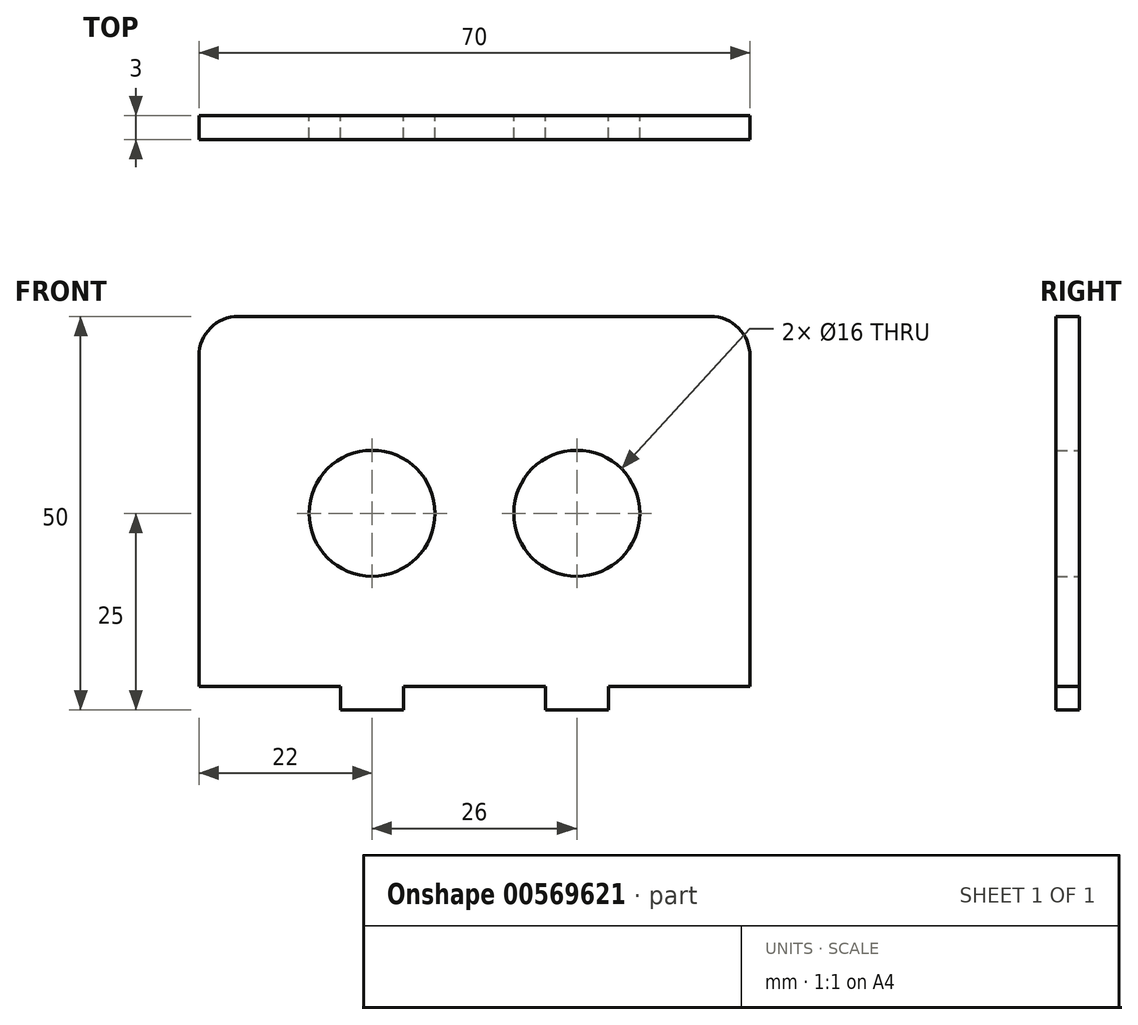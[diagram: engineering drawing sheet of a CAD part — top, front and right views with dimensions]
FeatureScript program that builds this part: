
annotation { "Feature Type Name" : "Feature", "Feature Type Description" : "" }
export const myFeature = defineFeature(function(context is Context, id is Id, definition is map)
    precondition{}
    {
        {
            var Q0;
            Q0=qCreatedBy(makeId("Front.planeOp"),FACE);
            var sketch = newSketch(context, id + "F0", { "sketchPlane" : qUnion([Q0])});
            skLineSegment(sketch, "E0.bottom", {"start": v(-30, 25) * mm, "end": v(30, 25) * mm});
            skLineSegment(sketch, "E0.top", {"start": v(-17, -25) * mm, "end": v(-9, -25) * mm});
            skLineSegment(sketch, "E0.left", {"start": v(-35, 20) * mm, "end": v(-35, -22) * mm});
            skLineSegment(sketch, "E0.right", {"start": v(35, 20) * mm, "end": v(35, -22) * mm});
            skLineSegment(sketch, "E1", {"start": v(-58.5, 0) * mm, "end": v(54.35, 0) * mm, "construction": true});
            skLineSegment(sketch, "E2", {"start": v(0, 37.83) * mm, "end": v(0, -35.44) * mm, "construction": true});
            skPoint(sketch, "E2.endSnap0", {"position": v(0, -25) * mm});
            skCircle(sketch, "E3", {"center": v(-13, 0) * mm, "radius": 8 * mm});
            skCircle(sketch, "E4", {"center": v(13, 0) * mm, "radius": 8 * mm});
            skPoint(sketch, "E5.visualSharp", {"position": v(-35, 25) * mm});
            skArc(sketch, "E5.filletArc", {"start": v(-30, 25) * mm, "mid": v(-33.54, 23.54) * mm, "end": v(-35, 20) * mm});
            skPoint(sketch, "E6.visualSharp", {"position": v(35, 25) * mm});
            skArc(sketch, "E6.filletArc", {"start": v(35, 20) * mm, "mid": v(33.54, 23.54) * mm, "end": v(30, 25) * mm});
            skLineSegment(sketch, "E7", {"start": v(-47.7, -22) * mm, "end": v(49.01, -22) * mm, "construction": true});
            skLineSegment(sketch, "E8", {"start": v(-35, -22) * mm, "end": v(-17, -22) * mm});
            skLineSegment(sketch, "E9", {"start": v(-17, -22) * mm, "end": v(-17, -25) * mm});
            skLineSegment(sketch, "E10", {"start": v(-9, -25) * mm, "end": v(-9, -22) * mm});
            skLineSegment(sketch, "E11", {"start": v(-9, -22) * mm, "end": v(9, -22) * mm});
            skLineSegment(sketch, "E12", {"start": v(9, -22) * mm, "end": v(9, -25) * mm});
            skLineSegment(sketch, "E13", {"start": v(9, -25) * mm, "end": v(17, -25) * mm});
            skLineSegment(sketch, "E14", {"start": v(17, -25) * mm, "end": v(17, -22) * mm});
            skLineSegment(sketch, "E15", {"start": v(17, -22) * mm, "end": v(35, -22) * mm});
            skPoint(sketch, "E16.orphan", {"position": v(-35, -25) * mm});
            skPoint(sketch, "E17.orphan", {"position": v(35, -25) * mm});
            skSolve(sketch);
        }
        {
            var Q0;
            Q0=makeQuery(id+"F0.imprint","IMPRINT",FACE,{"disambiguationData":[TD([[makeQuery(id+"F0.imprint","IMPRINT",EDGE,{"derivedFrom":sQuery(id+"F0.wireOp",EDGE,"E0.bottom")}),-1.0]])]});
            extrude(context, id + "F1", {"entities" : qUnion([Q0]), "depth" : 3 * mm, "offsetDistance" : 25 * mm});
        }
    });
